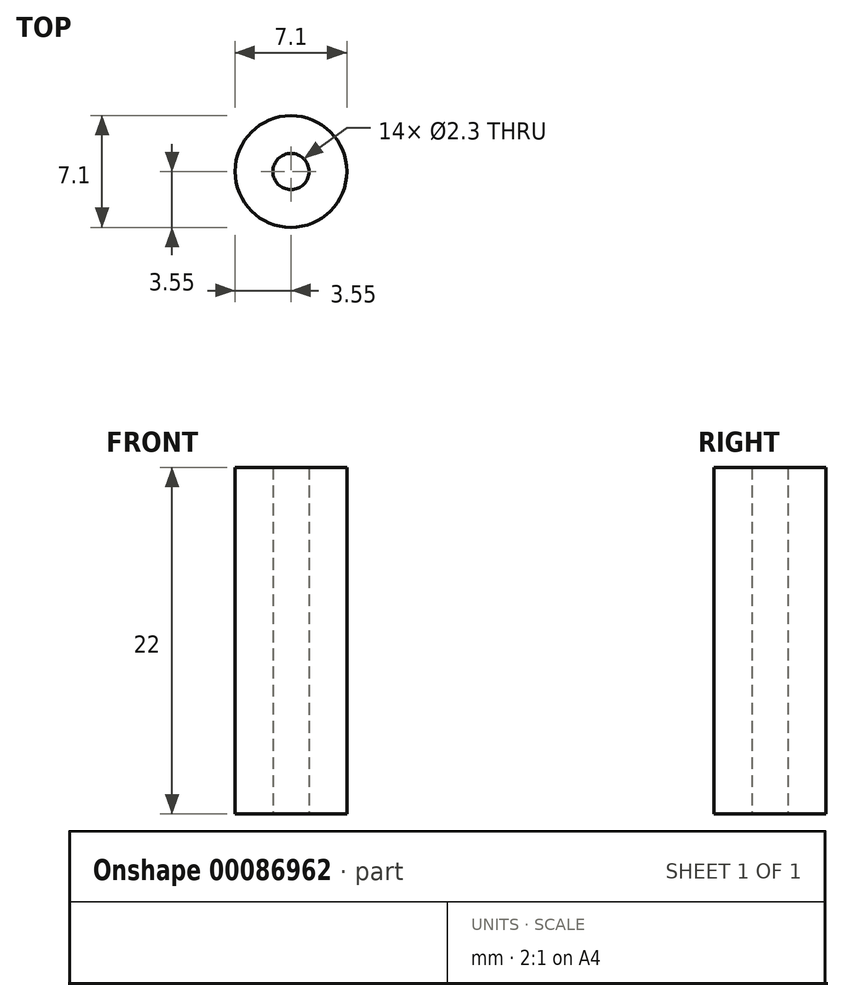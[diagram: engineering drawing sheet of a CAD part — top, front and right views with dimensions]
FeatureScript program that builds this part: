
annotation { "Feature Type Name" : "Feature", "Feature Type Description" : "" }
export const myFeature = defineFeature(function(context is Context, id is Id, definition is map)
    precondition{}
    {
        {
            var Q0;
            Q0=qCreatedBy(makeId("Top.planeOp"),FACE);
            var sketch = newSketch(context, id + "F0", { "sketchPlane" : qUnion([Q0])});
            skCircle(sketch, "E0", {"center": v(0, 0) * mm, "radius": 1.15 * mm});
            skCircle(sketch, "E1", {"center": v(0, 0) * mm, "radius": 3.55 * mm});
            skSolve(sketch);
        }
        {
            var Q0;
            Q0 = qSketchRegion(id + "F0", true);
            extrude(context, id + "F1", {"entities" : qUnion([Q0]), "depth" : 22 * mm});
        }
    });
